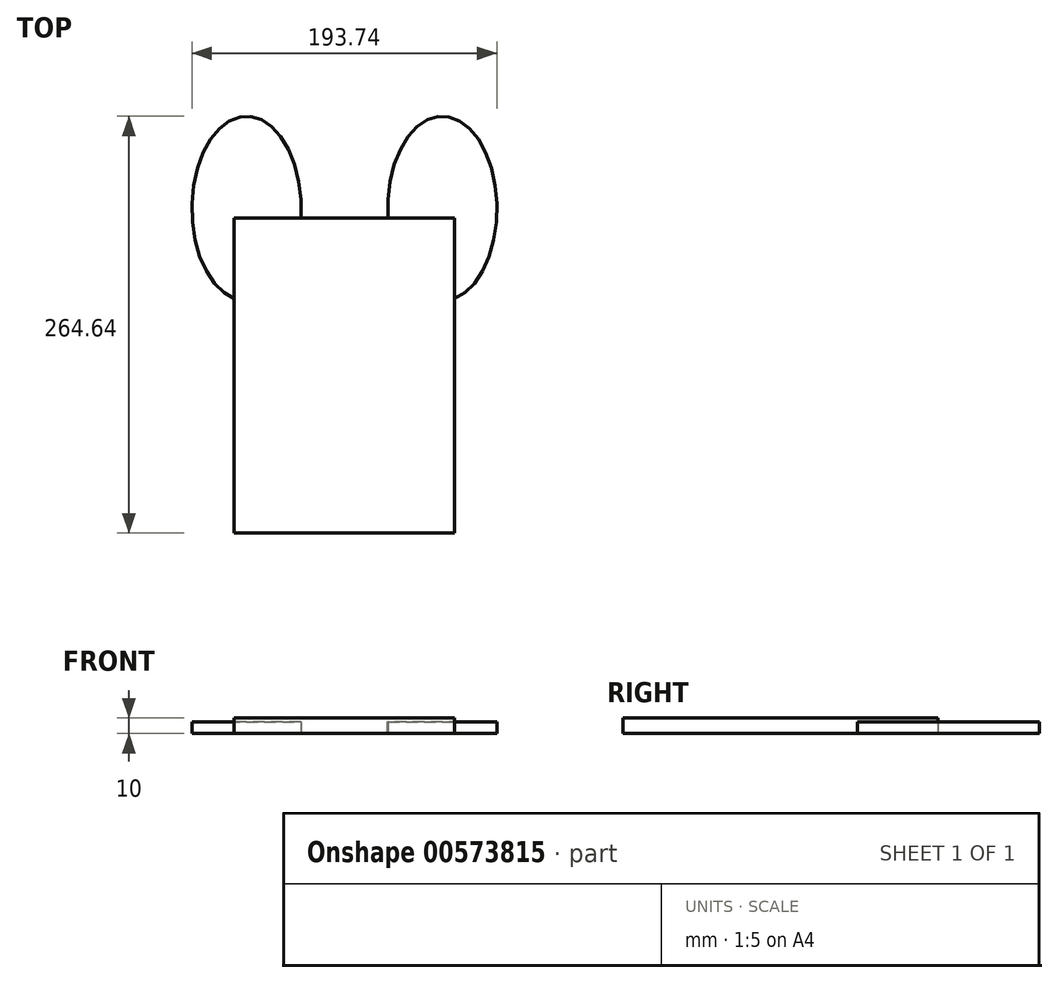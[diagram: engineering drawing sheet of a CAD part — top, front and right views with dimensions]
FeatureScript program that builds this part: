
annotation { "Feature Type Name" : "Feature", "Feature Type Description" : "" }
export const myFeature = defineFeature(function(context is Context, id is Id, definition is map)
    precondition{}
    {
        {
            var Q0;
            Q0=qCreatedBy(makeId("Top.planeOp"),FACE);
            var sketch = newSketch(context, id + "F0", { "sketchPlane" : qUnion([Q0])});
            skLineSegment(sketch, "E0.bottom", {"start": v(0, 0) * mm, "end": v(70, 0) * mm});
            skLineSegment(sketch, "E0.top", {"start": v(0, 200) * mm, "end": v(70, 200) * mm});
            skLineSegment(sketch, "E0.left", {"start": v(0, 0) * mm, "end": v(0, 200) * mm});
            skLineSegment(sketch, "E0.right", {"start": v(70, 0) * mm, "end": v(70, 200) * mm});
            skSolve(sketch);
        }
        {
            var Q0;
            Q0=makeQuery(id+"F0.imprint","IMPRINT",FACE,{"disambiguationData":[TD([[makeQuery(id+"F0.imprint","IMPRINT",EDGE,{"derivedFrom":sQuery(id+"F0.wireOp",EDGE,"E0.bottom")}),1.0]])]});
            var sketch = newSketch(context, id + "F1", { "sketchPlane" : qUnion([Q0])});
            skSolve(sketch);
        }
        {
            var Q0;
            Q0=makeQuery(id+"F1.imprint","IMPRINT",FACE,{"disambiguationData":[TD([[makeQuery(id+"F1.imprint","IMPRINT",EDGE,{"derivedFrom":makeQuery(id+"F0.imprint","IMPRINT",EDGE,{"derivedFrom":sQuery(id+"F0.wireOp",EDGE,"E0.bottom")})}),1.0]])]});
            extrude(context, id + "F2", {"entities" : qUnion([Q0]), "depth" : 10 * mm, "offsetDistance" : 25 * mm});
        }
        {
            var Q0;
            Q0=qCreatedBy(makeId("Top.planeOp"),FACE);
            var sketch = newSketch(context, id + "F3", { "sketchPlane" : qUnion([Q0])});
            skEllipse(sketch, "E1", {"center": v(62.17, 206.01) * mm, "majorRadius": 58.63 * mm, "minorRadius": 34.7 * mm, "majorAxis": v(0, 1)});
            skSolve(sketch);
        }
        {
            var Q0;
            Q0=makeQuery(id+"F3.imprint","IMPRINT",FACE,{"disambiguationData":[TD([[makeQuery(id+"F3.imprint","IMPRINT",EDGE,{"derivedFrom":sQuery(id+"F3.wireOp",EDGE,"E1")}),1.0]])]});
            extrude(context, id + "F4", {"entities" : qUnion([Q0]), "operationType" : NewBodyOperationType.ADD, "depth" : 7.5 * mm, "offsetDistance" : 25 * mm});
        }
        {
            var Q0;
            Q0=makeQuery(id+"F2.opExtrude","SWEPT_BODY",BODY,{"disambiguationData":[OSD([sQuery(id+"F0.wireOp",EDGE,"E0.bottom"),sQuery(id+"F0.wireOp",EDGE,"E0.top"),sQuery(id+"F0.wireOp",EDGE,"E0.left"),sQuery(id+"F0.wireOp",EDGE,"E0.right")])]});
            var Q1;
            Q1=qCreatedBy(makeId("Right.planeOp"),FACE);
            mirror(context, id + "F5", {"operationType" : NewBodyOperationType.ADD, "entities" : qUnion([Q0]), "mirrorPlane" : qUnion([Q1])});
        }
    });
